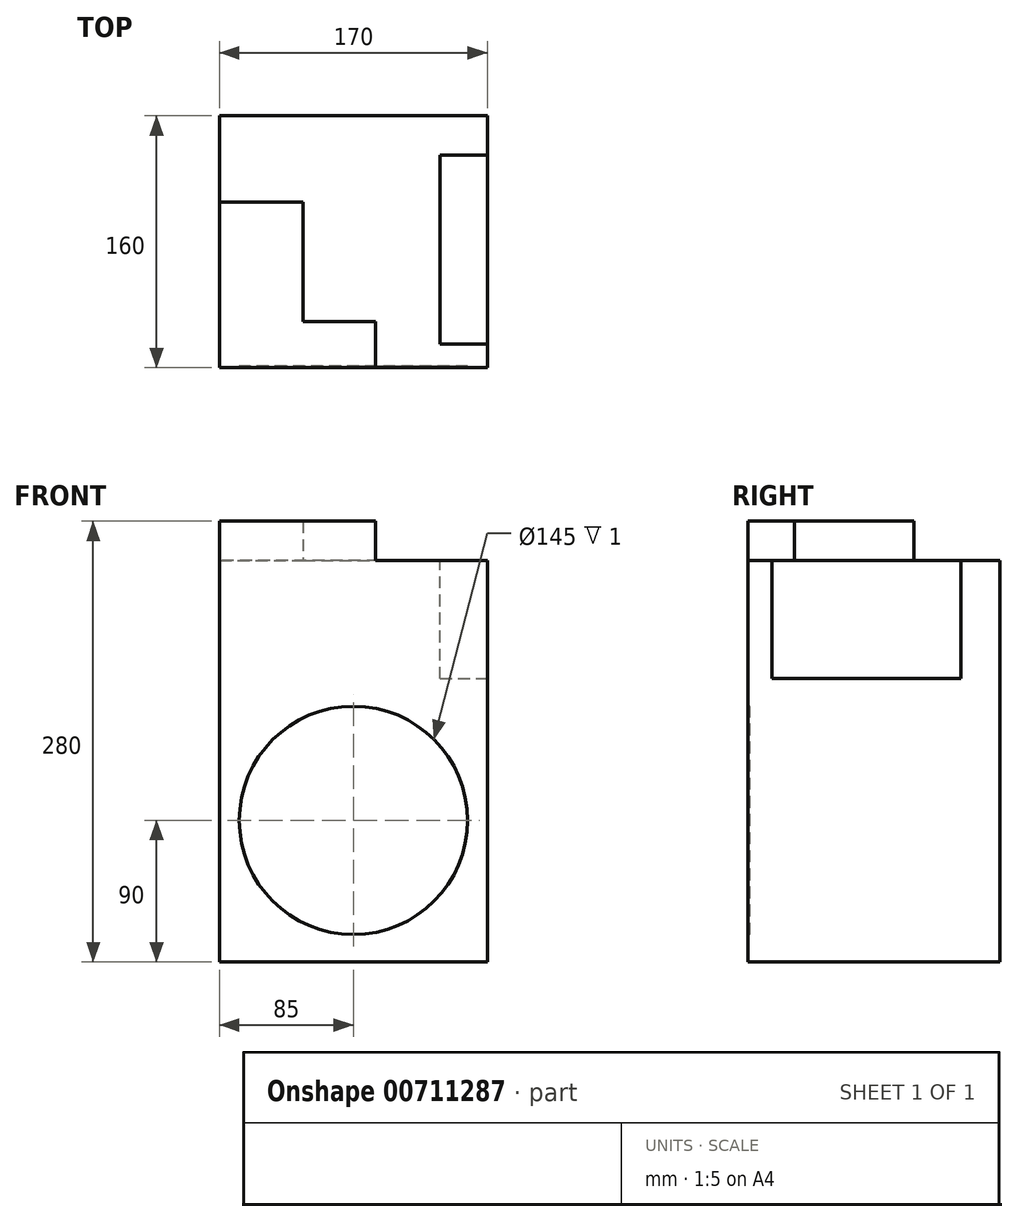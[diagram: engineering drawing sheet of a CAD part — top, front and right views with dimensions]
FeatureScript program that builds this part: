
annotation { "Feature Type Name" : "Feature", "Feature Type Description" : "" }
export const myFeature = defineFeature(function(context is Context, id is Id, definition is map)
    precondition{}
    {
        {
            var Q0;
            Q0=qCreatedBy(makeId("Front.planeOp"),FACE);
            var sketch = newSketch(context, id + "F0", { "sketchPlane" : qUnion([Q0])});
            skLineSegment(sketch, "E0.bottom", {"start": v(85, 127.5) * mm, "end": v(-85, 127.5) * mm});
            skLineSegment(sketch, "E0.top", {"start": v(85, -127.5) * mm, "end": v(-85, -127.5) * mm});
            skLineSegment(sketch, "E0.left", {"start": v(85, 127.5) * mm, "end": v(85, -127.5) * mm});
            skLineSegment(sketch, "E0.right", {"start": v(-85, 127.5) * mm, "end": v(-85, -127.5) * mm});
            skPoint(sketch, "E0.middle", {"position": v(0, 0) * mm});
            skSolve(sketch);
        }
        {
            var Q0;
            Q0 = qSketchRegion(id + "F0", true);
            extrude(context, id + "F1", {"entities" : qUnion([Q0]), "depth" : 160 * mm, "offsetDistance" : 25 * mm});
        }
        {
            var Q0;
            Q0=makeQuery(id+"F1.opExtrude","CAP_FACE",FACE,{"disambiguationData":[OSD([sQuery(id+"F0.wireOp",EDGE,"E0.bottom"),sQuery(id+"F0.wireOp",EDGE,"E0.top"),sQuery(id+"F0.wireOp",EDGE,"E0.left"),sQuery(id+"F0.wireOp",EDGE,"E0.right")])],"isStart":false});
            var sketch = newSketch(context, id + "F2", { "sketchPlane" : qUnion([Q0])});
            skLineSegment(sketch, "E1", {"start": v(0, 127.5) * mm, "end": v(0, -127.5) * mm, "construction": true});
            skLineSegment(sketch, "E2", {"start": v(-85, -37.5) * mm, "end": v(85, -37.5) * mm, "construction": true});
            skCircle(sketch, "E3", {"center": v(0, -37.5) * mm, "radius": 72.5 * mm});
            skSolve(sketch);
        }
        {
            var Q0;
            Q0 = qSketchRegion(id + "F2", true);
            extrude(context, id + "F3", {"entities" : qUnion([Q0]), "operationType" : NewBodyOperationType.REMOVE, "oppositeDirection" : true, "depth" : 1 * mm, "offsetDistance" : 25 * mm});
        }
        {
            var Q0;
            Q0=makeQuery(id+"F1.opExtrude","SWEPT_FACE",FACE,{"disambiguationData":[OSD([sQuery(id+"F0.wireOp",EDGE,"E0.left")])]});
            var sketch = newSketch(context, id + "F4", { "sketchPlane" : qUnion([Q0])});
            skLineSegment(sketch, "E4.bottom", {"start": v(-145, 52.5) * mm, "end": v(-25, 52.5) * mm});
            skLineSegment(sketch, "E4.top", {"start": v(-145, 127.5) * mm, "end": v(-25, 127.5) * mm});
            skLineSegment(sketch, "E4.left", {"start": v(-145, 52.5) * mm, "end": v(-145, 127.5) * mm});
            skLineSegment(sketch, "E4.right", {"start": v(-25, 52.5) * mm, "end": v(-25, 127.5) * mm});
            skSolve(sketch);
        }
        {
            var Q0;
            Q0 = qSketchRegion(id + "F4", true);
            extrude(context, id + "F5", {"entities" : qUnion([Q0]), "operationType" : NewBodyOperationType.REMOVE, "oppositeDirection" : true, "depth" : 30 * mm, "offsetDistance" : 25 * mm});
        }
        {
            var Q0;
            Q0=makeQuery(id+"F1.opExtrude","SWEPT_FACE",FACE,{"disambiguationData":[OSD([sQuery(id+"F0.wireOp",EDGE,"E0.bottom")])]});
            var sketch = newSketch(context, id + "F6", { "sketchPlane" : qUnion([Q0])});
            skLineSegment(sketch, "E5.bottom", {"start": v(-85, -160) * mm, "end": v(13.92, -160) * mm});
            skLineSegment(sketch, "E5.top", {"start": v(-31.84, -130.73) * mm, "end": v(13.92, -130.73) * mm});
            skLineSegment(sketch, "E5.left", {"start": v(-85, -160) * mm, "end": v(-85, -130.73) * mm});
            skLineSegment(sketch, "E5.right", {"start": v(13.92, -160) * mm, "end": v(13.92, -130.73) * mm});
            skLineSegment(sketch, "E6.top", {"start": v(-85, -54.68) * mm, "end": v(-31.84, -54.68) * mm});
            skLineSegment(sketch, "E6.left", {"start": v(-85, -130.73) * mm, "end": v(-85, -54.68) * mm});
            skLineSegment(sketch, "E6.right", {"start": v(-31.84, -130.73) * mm, "end": v(-31.84, -54.68) * mm});
            skSolve(sketch);
        }
        {
            var Q0;
            Q0 = qSketchRegion(id + "F6", true);
            extrude(context, id + "F7", {"entities" : qUnion([Q0]), "operationType" : NewBodyOperationType.ADD, "depth" : 25 * mm, "offsetDistance" : 25 * mm});
        }
    });
